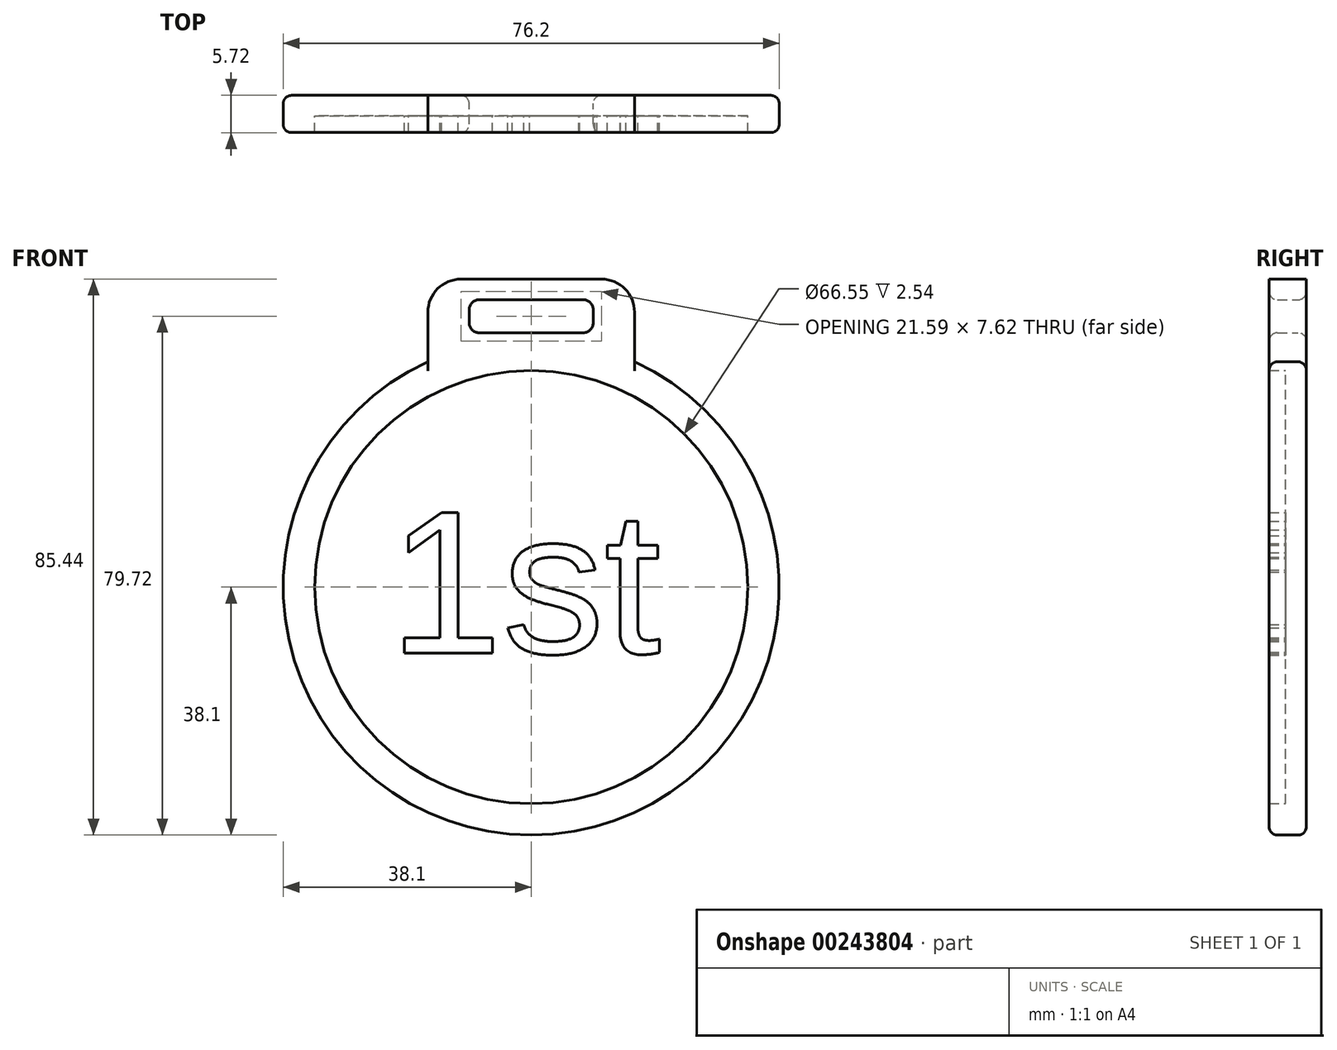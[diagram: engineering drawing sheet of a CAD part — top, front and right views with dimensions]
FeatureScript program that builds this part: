
annotation { "Feature Type Name" : "Feature", "Feature Type Description" : "" }
export const myFeature = defineFeature(function(context is Context, id is Id, definition is map)
    precondition{}
    {
        {
            var Q0;
            Q0=qCreatedBy(makeId("Front.planeOp"),FACE);
            var sketch = newSketch(context, id + "F0", { "sketchPlane" : qUnion([Q0])});
            skCircle(sketch, "E0", {"center": v(0, 0) * mm, "radius": 38.1 * mm});
            skSolve(sketch);
        }
        {
            var Q0;
            Q0 = qSketchRegion(id + "F0", true);
            extrude(context, id + "F1", {"entities" : qUnion([Q0]), "depth" : 3.17 * mm});
        }
        {
            var Q0;
            Q0=makeQuery(id+"F1.opExtrude","CAP_FACE",FACE,{"disambiguationData":[OSD([sQuery(id+"F0.wireOp",EDGE,"E0")])],"isStart":false});
            var sketch = newSketch(context, id + "F2", { "sketchPlane" : qUnion([Q0])});
            skCircle(sketch, "E1.0.0", {"center": v(0, 0) * mm, "radius": 38.1 * mm});
            skCircle(sketch, "E2.0", {"center": v(0, 0) * mm, "radius": 33.27 * mm});
            skSolve(sketch);
        }
        {
            var Q0;
            Q0 = qSketchRegion(id + "F2", true);
            extrude(context, id + "F3", {"entities" : qUnion([Q0]), "operationType" : NewBodyOperationType.ADD, "depth" : 2.54 * mm});
        }
        {
            var Q0;
            Q0=makeQuery(id+"F1.opExtrude","CAP_FACE",FACE,{"disambiguationData":[OSD([sQuery(id+"F0.wireOp",EDGE,"E0")])],"isStart":false});
            var sketch = newSketch(context, id + "F4", { "sketchPlane" : qUnion([Q0])});
            skText(sketch, "E3", { "text": "1st", "fontName": "Arimo-Regular.ttf"});
            const initialGuessF4  = {"E3": [-0.0219, -0.01015, 1, 0, 0.02259]};
            skSetInitialGuess(sketch, initialGuessF4);
            skSolve(sketch);
        }
        {
            var Q0;
            Q0=makeQuery(id+"F4.imprint","IMPRINT",FACE,{"disambiguationData":[TD([[makeQuery(id+"F4.imprint","IMPRINT",EDGE,{"derivedFrom":sQuery(id+"F4.wireOp",EDGE,"E3.sketch_text.stroke-0")}),-1.0]])]});
            var Q1;
            Q1=makeQuery(id+"F4.imprint","IMPRINT",FACE,{"disambiguationData":[TD([[makeQuery(id+"F4.imprint","IMPRINT",EDGE,{"derivedFrom":sQuery(id+"F4.wireOp",EDGE,"E3.sketch_text.stroke-11")}),-1.0]])]});
            var Q2;
            Q2=makeQuery(id+"F4.imprint","IMPRINT",FACE,{"disambiguationData":[TD([[makeQuery(id+"F4.imprint","IMPRINT",EDGE,{"derivedFrom":sQuery(id+"F4.wireOp",EDGE,"E3.sketch_text.stroke-42")}),-1.0]])]});
            var Q3;
            Q3=makeQuery(id+"F3.opExtrude","CAP_FACE",FACE,{"disambiguationData":[OSD([sQuery(id+"F2.wireOp",EDGE,"E1.0.0"),sQuery(id+"F2.wireOp",EDGE,"E2.0")])],"isStart":false});
            extrude(context, id + "F5", {"entities" : qUnion([Q0, Q1, Q2]), "operationType" : NewBodyOperationType.ADD, "endBound" : BoundingType.UP_TO_SURFACE, "endBoundEntityFace" : qUnion([Q3]), "depth" : 2.54 * mm});
        }
        {
            var Q0;
            Q0=qCreatedBy(makeId("Front.planeOp"),FACE);
            var sketch = newSketch(context, id + "F6", { "sketchPlane" : qUnion([Q0])});
            skLineSegment(sketch, "E4", {"start": v(-15.87, 47.34) * mm, "end": v(-15.87, 34.64) * mm});
            skLineSegment(sketch, "E5.MirrorCS", {"start": v(15.87, 47.34) * mm, "end": v(15.88, 34.64) * mm});
            skLineSegment(sketch, "E6", {"start": v(-15.88, 47.34) * mm, "end": v(15.88, 47.34) * mm});
            skArc(sketch, "E7", {"start": v(-15.87, 34.64) * mm, "mid": v(0, 38.1) * mm, "end": v(15.88, 34.64) * mm});
            skLineSegment(sketch, "E8.bottom", {"start": v(-9.53, 44.16) * mm, "end": v(9.53, 44.16) * mm});
            skLineSegment(sketch, "E8.top", {"start": v(-9.53, 39.08) * mm, "end": v(9.53, 39.08) * mm});
            skLineSegment(sketch, "E8.left", {"start": v(-9.53, 44.16) * mm, "end": v(-9.53, 39.08) * mm});
            skLineSegment(sketch, "E8.right", {"start": v(9.53, 44.16) * mm, "end": v(9.53, 39.08) * mm});
            skSolve(sketch);
        }
        {
            var Q0;
            Q0=makeQuery(id+"F6.imprint","IMPRINT",FACE,{"disambiguationData":[TD([[makeQuery(id+"F6.imprint","IMPRINT",EDGE,{"derivedFrom":sQuery(id+"F6.wireOp",EDGE,"E4")}),1.0]])]});
            var Q1;
            Q1=makeQuery(id+"F3.opExtrude","CAP_FACE",FACE,{"disambiguationData":[OSD([sQuery(id+"F2.wireOp",EDGE,"E1.0.0"),sQuery(id+"F2.wireOp",EDGE,"E2.0")])],"isStart":false});
            extrude(context, id + "F7", {"entities" : qUnion([Q0]), "operationType" : NewBodyOperationType.ADD, "endBound" : BoundingType.UP_TO_SURFACE, "endBoundEntityFace" : qUnion([Q1]), "depth" : 25.4 * mm});
        }
        {
            var Q0;
            Q0=makeQuery(id+"F7.opExtrude","SWEPT_EDGE",EDGE,{"disambiguationData":[OSD([sQuery(id+"F6.wireOp",EDGE,"E5.MirrorCS"),sQuery(id+"F6.wireOp",EDGE,"E7")])]});
            var Q1;
            Q1=makeQuery(id+"F7.opExtrude","SWEPT_EDGE",EDGE,{"disambiguationData":[OSD([sQuery(id+"F6.wireOp",EDGE,"E4"),sQuery(id+"F6.wireOp",EDGE,"E7")])]});
            var Q2;
            Q2=makeQuery(id+"F7.opExtrude","SWEPT_EDGE",EDGE,{"disambiguationData":[OSD([sQuery(id+"F6.wireOp",EDGE,"E4"),sQuery(id+"F6.wireOp",EDGE,"E6")])]});
            var Q3;
            Q3=makeQuery(id+"F7.opExtrude","SWEPT_EDGE",EDGE,{"disambiguationData":[OSD([sQuery(id+"F6.wireOp",EDGE,"E5.MirrorCS"),sQuery(id+"F6.wireOp",EDGE,"E6")])]});
            fillet(context, id + "F8", {"entities" : qUnion([Q0, Q1, Q2, Q3]), "radius" : 5.08 * mm, "tangentPropagation" : true, "allowEdgeOverflow" : false});
        }
        {
            var Q0;
            Q0=makeQuery(id+"F7.opExtrude","SWEPT_EDGE",EDGE,{"disambiguationData":[OSD([sQuery(id+"F6.wireOp",EDGE,"E8.top"),sQuery(id+"F6.wireOp",EDGE,"E8.left")])]});
            var Q1;
            Q1=makeQuery(id+"F7.opExtrude","SWEPT_EDGE",EDGE,{"disambiguationData":[OSD([sQuery(id+"F6.wireOp",EDGE,"E8.bottom"),sQuery(id+"F6.wireOp",EDGE,"E8.left")])]});
            var Q2;
            Q2=makeQuery(id+"F7.opExtrude","SWEPT_EDGE",EDGE,{"disambiguationData":[OSD([sQuery(id+"F6.wireOp",EDGE,"E8.bottom"),sQuery(id+"F6.wireOp",EDGE,"E8.right")])]});
            var Q3;
            Q3=makeQuery(id+"F7.opExtrude","SWEPT_EDGE",EDGE,{"disambiguationData":[OSD([sQuery(id+"F6.wireOp",EDGE,"E8.top"),sQuery(id+"F6.wireOp",EDGE,"E8.right")])]});
            fillet(context, id + "F9", {"entities" : qUnion([Q0, Q1, Q2, Q3]), "radius" : 1.52 * mm, "tangentPropagation" : true, "allowEdgeOverflow" : false});
        }
        {
            var Q0;
            Q0=makeQuery(id+"F3.opExtrude","CAP_EDGE",EDGE,{"disambiguationData":[OSD([sQuery(id+"F2.wireOp",EDGE,"E1.0.0")])],"isStart":false});
            var Q1;
            Q1=makeQuery(id+"F1.opExtrude","CAP_EDGE",EDGE,{"disambiguationData":[OSD([sQuery(id+"F0.wireOp",EDGE,"E0")])],"isStart":true});
            var Q2;
            Q2=makeQuery(id+"F7.opExtrude","CAP_EDGE",EDGE,{"disambiguationData":[OSD([sQuery(id+"F6.wireOp",EDGE,"E8.top")])],"isStart":false});
            var Q3;
            Q3=makeQuery(id+"F7.opExtrude","CAP_EDGE",EDGE,{"disambiguationData":[OSD([sQuery(id+"F6.wireOp",EDGE,"E8.top")])],"isStart":true});
            fillet(context, id + "F10", {"entities" : qUnion([Q0, Q1, Q2, Q3]), "radius" : 1.27 * mm, "tangentPropagation" : true, "allowEdgeOverflow" : false});
        }
    });
